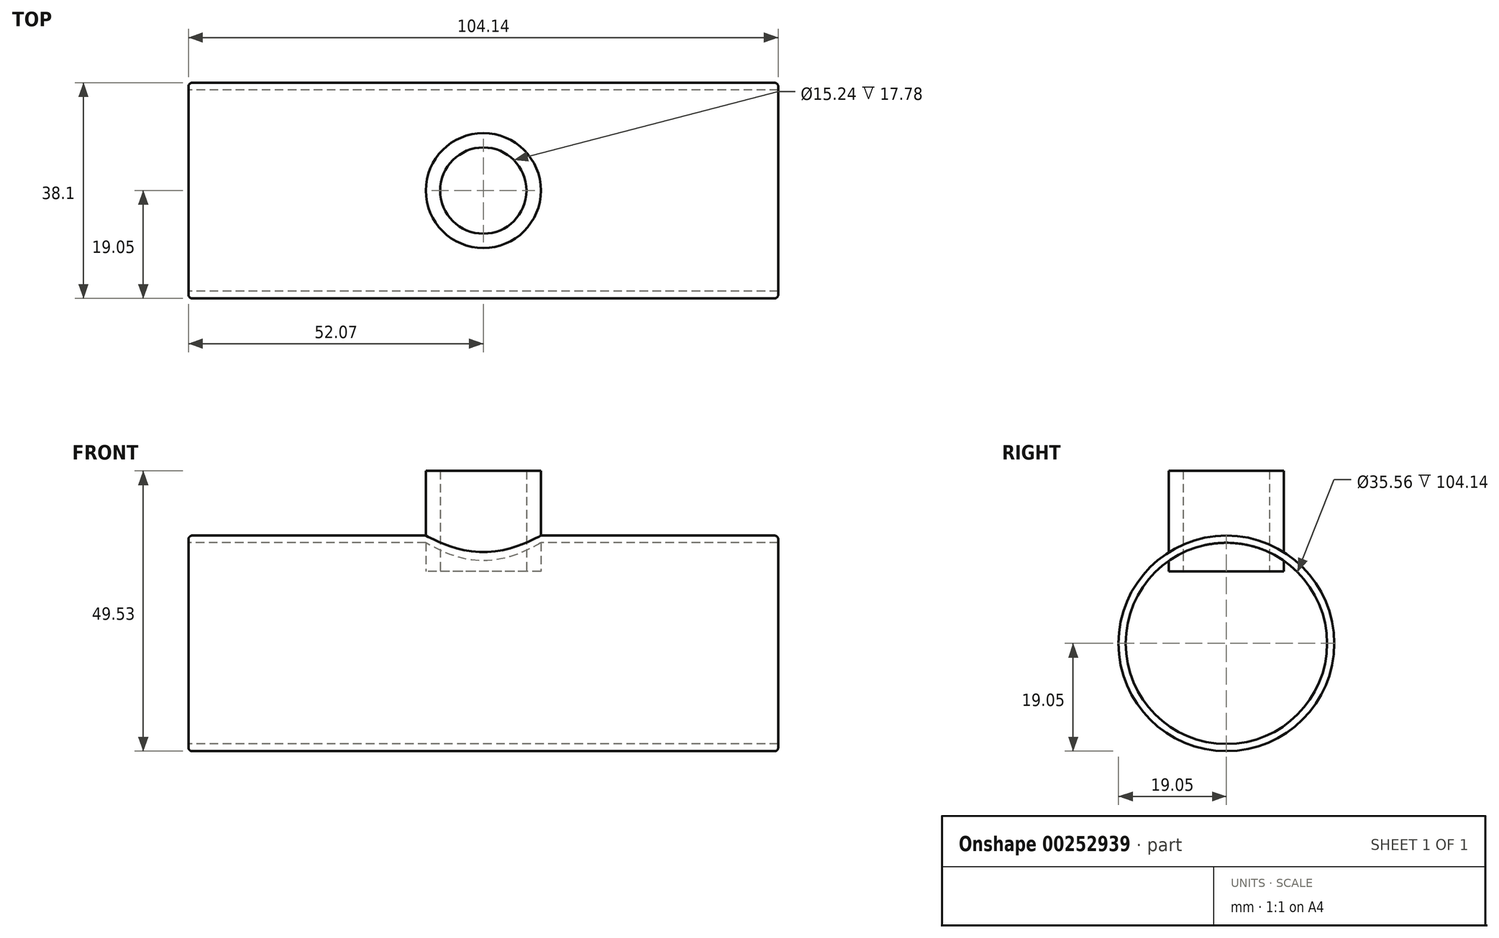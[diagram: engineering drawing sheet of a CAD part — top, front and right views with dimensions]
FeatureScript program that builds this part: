
annotation { "Feature Type Name" : "Feature", "Feature Type Description" : "" }
export const myFeature = defineFeature(function(context is Context, id is Id, definition is map)
    precondition{}
    {
        {
            var Q0;
            Q0=qCreatedBy(makeId("Right.planeOp"),FACE);
            var sketch = newSketch(context, id + "F0", { "sketchPlane" : qUnion([Q0])});
            skCircle(sketch, "E0", {"center": v(0, 0) * mm, "radius": 17.78 * mm});
            skCircle(sketch, "E1", {"center": v(0, 0) * mm, "radius": 19.05 * mm});
            skSolve(sketch);
        }
        {
            var Q0;
            Q0 = qSketchRegion(id + "F0", true);
            extrude(context, id + "F1", {"entities" : qUnion([Q0]), "endBound" : BoundingType.SYMMETRIC, "depth" : 104.14 * mm});
        }
        {
            var Q0;
            Q0=makeQuery(id+"F1.opExtrude","CAP_EDGE",EDGE,{"disambiguationData":[OSD([sQuery(id+"F0.wireOp",EDGE,"E1")])],"isStart":false});
            var Q1;
            Q1=makeQuery(id+"F1.opExtrude","CAP_EDGE",EDGE,{"disambiguationData":[OSD([sQuery(id+"F0.wireOp",EDGE,"E1")])],"isStart":true});
            fillet(context, id + "F2", {"entities" : qUnion([Q0, Q1]), "radius" : 0.64 * mm, "tangentPropagation" : true, "allowEdgeOverflow" : false});
        }
        {
            var Q0;
            Q0=qCreatedBy(makeId("Top.planeOp"),FACE);
            var sketch = newSketch(context, id + "F3", { "sketchPlane" : qUnion([Q0])});
            skCircle(sketch, "E2", {"center": v(0, 0) * mm, "radius": 10.16 * mm});
            skCircle(sketch, "E3", {"center": v(0, 0) * mm, "radius": 7.62 * mm});
            skSolve(sketch);
        }
        {
            var Q0;
            Q0 = qSketchRegion(id + "F3", true);
            extrude(context, id + "F4", {"entities" : qUnion([Q0]), "operationType" : NewBodyOperationType.ADD, "depth" : 30.48 * mm});
        }
        {
            var Q0;
            Q0=qCreatedBy(makeId("Top.planeOp"),FACE);
            var sketch = newSketch(context, id + "F5", { "sketchPlane" : qUnion([Q0])});
            skCircle(sketch, "E4", {"center": v(0, 0) * mm, "radius": 7.62 * mm});
            skSolve(sketch);
        }
        {
            var Q0;
            Q0 = qSketchRegion(id + "F5", true);
            extrude(context, id + "F6", {"entities" : qUnion([Q0]), "operationType" : NewBodyOperationType.REMOVE, "endBound" : BoundingType.THROUGH_ALL, "depth" : 5.08 * mm});
        }
        {
            var Q0;
            Q0=qCreatedBy(makeId("Right.planeOp"),FACE);
            var sketch = newSketch(context, id + "F7", { "sketchPlane" : qUnion([Q0])});
            skArc(sketch, "E5", {"start": v(-10.16, 14.6) * mm, "mid": v(0, -17.78) * mm, "end": v(10.16, 14.6) * mm});
            skLineSegment(sketch, "E6", {"start": v(-10.16, 12.7) * mm, "end": v(10.16, 12.7) * mm});
            skLineSegment(sketch, "E7", {"start": v(-10.16, 14.6) * mm, "end": v(-10.16, 12.7) * mm});
            skLineSegment(sketch, "E8", {"start": v(10.16, 12.7) * mm, "end": v(10.16, 14.6) * mm});
            skPoint(sketch, "E9.MirrorCS.end.orphan", {"position": v(10.16, 0) * mm});
            skSolve(sketch);
        }
        {
            var Q0;
            Q0 = qSketchRegion(id + "F7", true);
            extrude(context, id + "F8", {"entities" : qUnion([Q0]), "operationType" : NewBodyOperationType.REMOVE, "endBound" : BoundingType.SYMMETRIC, "depth" : 50.8 * mm});
        }
    });
